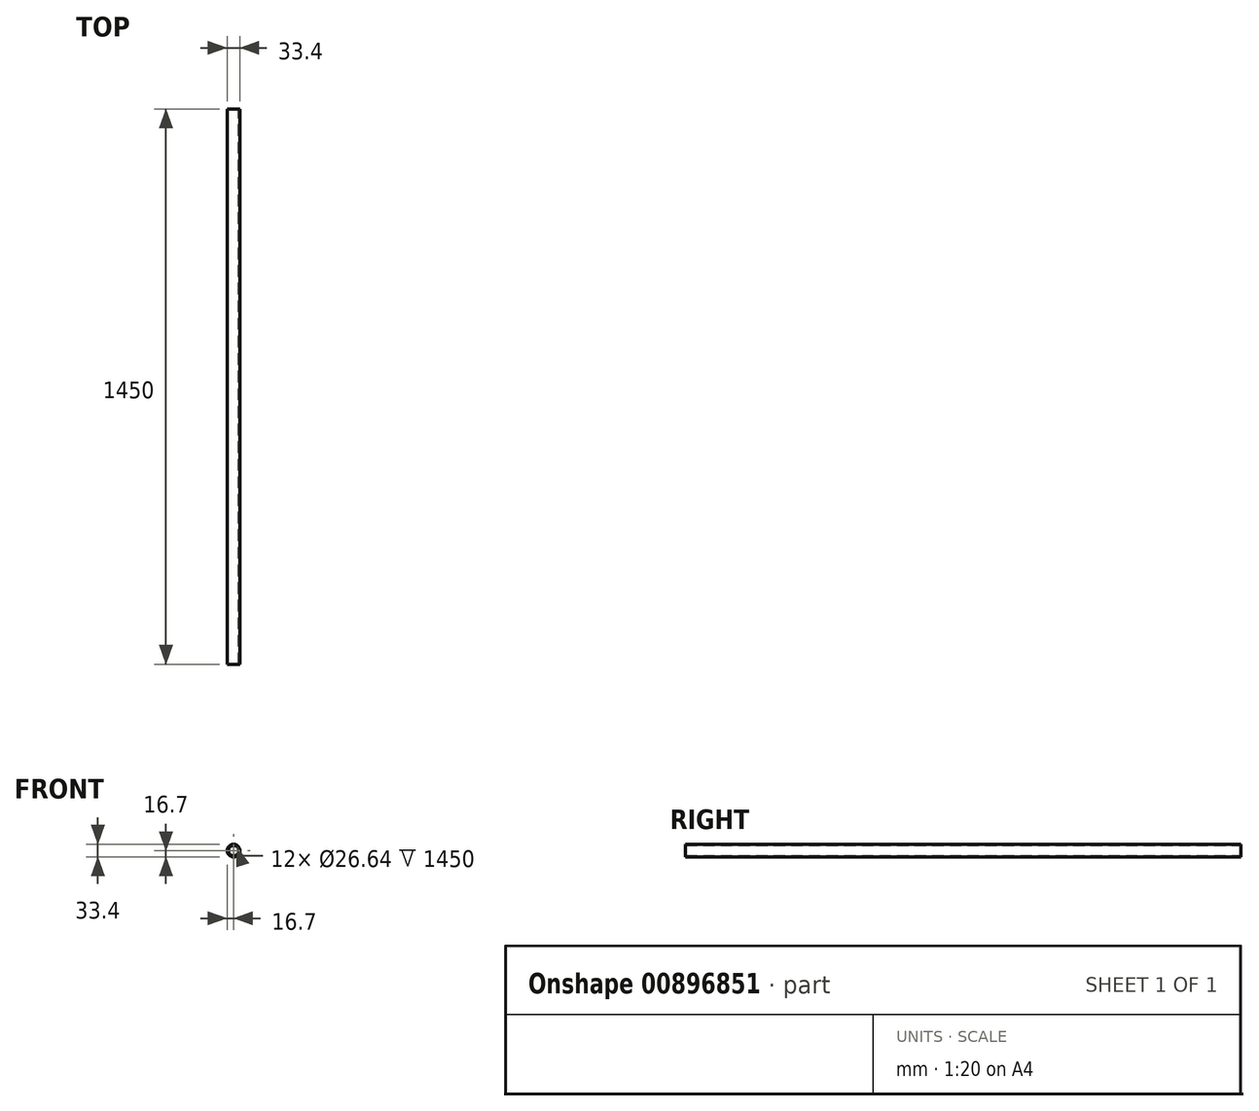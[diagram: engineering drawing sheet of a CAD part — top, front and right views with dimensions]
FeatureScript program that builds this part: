
annotation { "Feature Type Name" : "Feature", "Feature Type Description" : "" }
export const myFeature = defineFeature(function(context is Context, id is Id, definition is map)
    precondition{}
    {
        {
            var Q0;
            Q0=qCreatedBy(makeId("Front.planeOp"),FACE);
            var sketch = newSketch(context, id + "F0", { "sketchPlane" : qUnion([Q0])});
            skCircle(sketch, "E0", {"center": v(0, 0) * mm, "radius": 16.7 * mm});
            skCircle(sketch, "E1", {"center": v(0, 0) * mm, "radius": 13.32 * mm});
            skSolve(sketch);
        }
        {
            var Q0;
            Q0=makeQuery(id+"F0.imprint","IMPRINT",FACE,{"disambiguationData":[TD([[makeQuery(id+"F0.imprint","IMPRINT",EDGE,{"derivedFrom":sQuery(id+"F0.wireOp",EDGE,"E0")}),1.0]])]});
            extrude(context, id + "F1", {"entities" : qUnion([Q0]), "endBound" : BoundingType.SYMMETRIC, "depth" : 1450 * mm, "offsetDistance" : 25.4 * mm});
        }
    });
